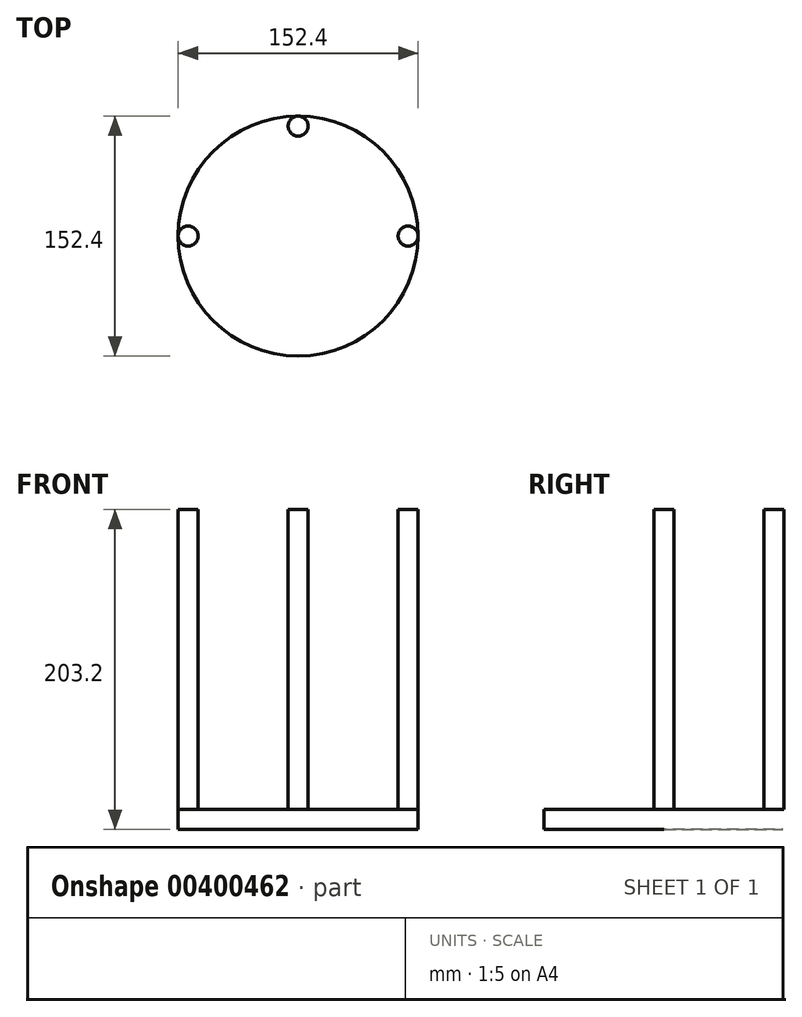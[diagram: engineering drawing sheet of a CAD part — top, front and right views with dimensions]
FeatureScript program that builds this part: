
annotation { "Feature Type Name" : "Feature", "Feature Type Description" : "" }
export const myFeature = defineFeature(function(context is Context, id is Id, definition is map)
    precondition{}
    {
        {
            var Q0;
            Q0=qCreatedBy(makeId("Top.planeOp"),FACE);
            var sketch = newSketch(context, id + "F0", { "sketchPlane" : qUnion([Q0])});
            skCircle(sketch, "E0", {"center": v(0, 0) * mm, "radius": 76.2 * mm});
            skSolve(sketch);
        }
        {
            var Q0;
            Q0 = qSketchRegion(id + "F0", true);
            extrude(context, id + "F1", {"entities" : qUnion([Q0]), "depth" : 12.7 * mm});
        }
        {
            var Q0;
            Q0=makeQuery(id+"F1.opExtrude","CAP_FACE",FACE,{"disambiguationData":[OSD([sQuery(id+"F0.wireOp",EDGE,"E0")])],"isStart":false});
            var sketch = newSketch(context, id + "F2", { "sketchPlane" : qUnion([Q0])});
            skCircle(sketch, "E1", {"center": v(0, 69.85) * mm, "radius": 6.35 * mm});
            skCircle(sketch, "E2", {"center": v(-69.85, 0) * mm, "radius": 6.35 * mm});
            skCircle(sketch, "E3", {"center": v(69.85, 0) * mm, "radius": 6.35 * mm});
            skSolve(sketch);
        }
        {
            var Q0;
            Q0=makeQuery(id+"F2.imprint","IMPRINT",FACE,{"disambiguationData":[TD([[makeQuery(id+"F2.imprint","IMPRINT",EDGE,{"derivedFrom":sQuery(id+"F2.wireOp",EDGE,"E2")}),1.0]])]});
            var Q1;
            Q1=makeQuery(id+"F2.imprint","IMPRINT",FACE,{"disambiguationData":[TD([[makeQuery(id+"F2.imprint","IMPRINT",EDGE,{"derivedFrom":sQuery(id+"F2.wireOp",EDGE,"E1")}),1.0]])]});
            var Q2;
            Q2=makeQuery(id+"F2.imprint","IMPRINT",FACE,{"disambiguationData":[TD([[makeQuery(id+"F2.imprint","IMPRINT",EDGE,{"derivedFrom":sQuery(id+"F2.wireOp",EDGE,"E3")}),1.0]])]});
            extrude(context, id + "F3", {"entities" : qUnion([Q0, Q1, Q2]), "operationType" : NewBodyOperationType.ADD, "depth" : 190.5 * mm});
        }
    });
